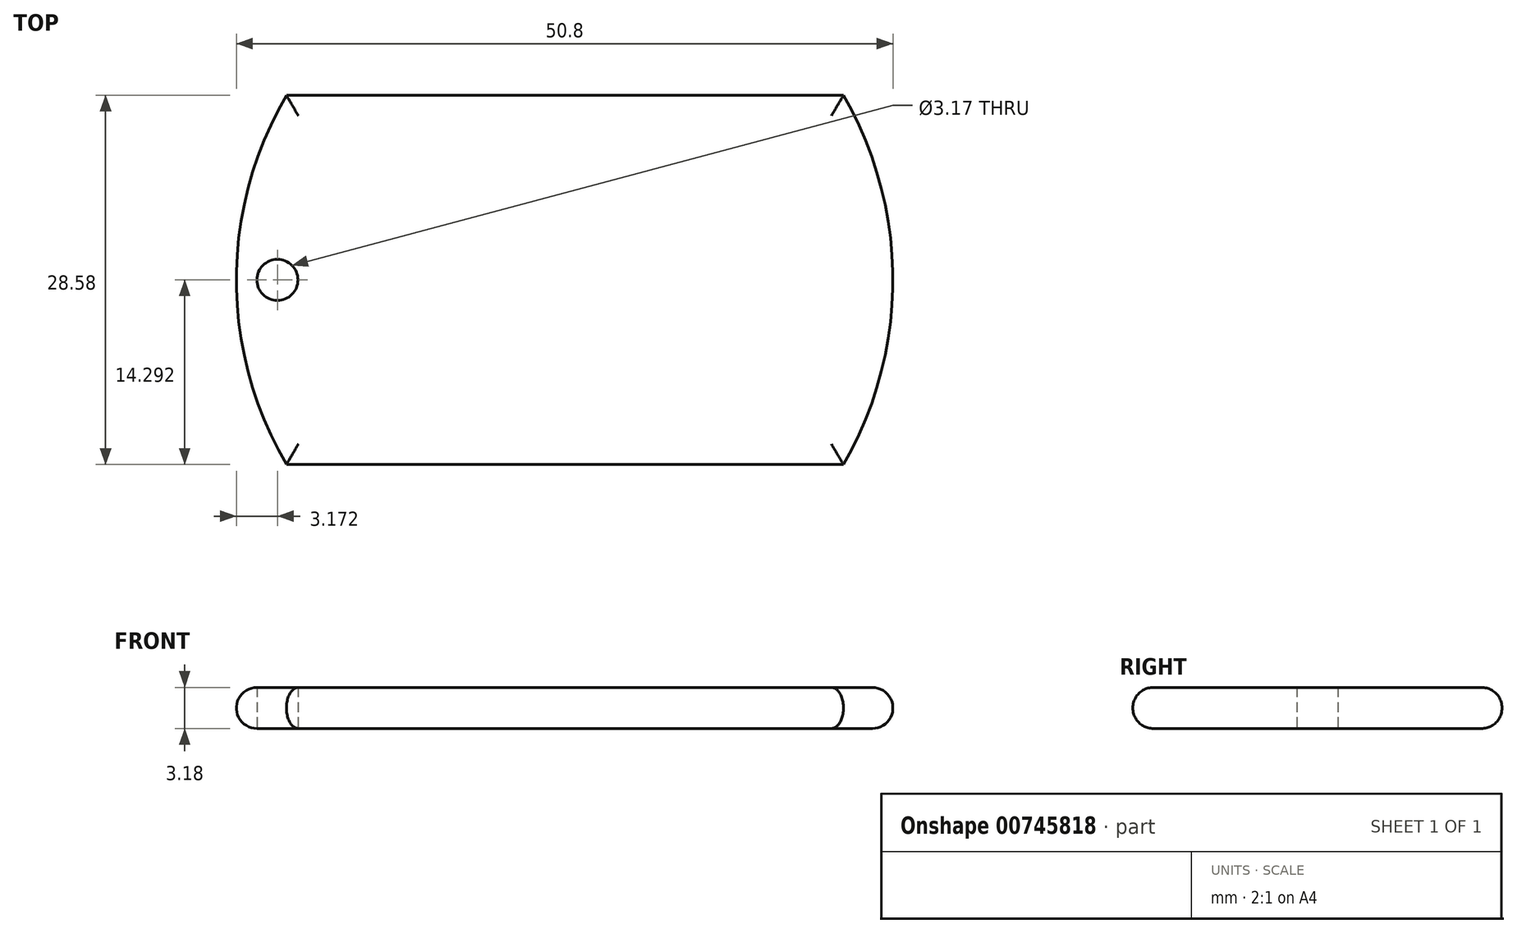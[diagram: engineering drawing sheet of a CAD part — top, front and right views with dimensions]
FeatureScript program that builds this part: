
annotation { "Feature Type Name" : "Feature", "Feature Type Description" : "" }
export const myFeature = defineFeature(function(context is Context, id is Id, definition is map)
    precondition{}
    {
        {
            var Q0;
            Q0=qCreatedBy(makeId("Top.planeOp"),FACE);
            var sketch = newSketch(context, id + "F0", { "sketchPlane" : qUnion([Q0])});
            skLineSegment(sketch, "E0.bottom", {"start": v(21.55, 14.35) * mm, "end": v(0, 14.35) * mm});
            skLineSegment(sketch, "E0.top", {"start": v(21.55, -14.23) * mm, "end": v(0, -14.23) * mm});
            skPoint(sketch, "E0.middle", {"position": v(0, 0) * mm});
            skArc(sketch, "E1", {"start": v(21.55, -14.23) * mm, "mid": v(25.38, 0.06) * mm, "end": v(21.55, 14.35) * mm});
            skLineSegment(sketch, "E2.MirrorCS", {"start": v(-21.55, -14.23) * mm, "end": v(0, -14.23) * mm});
            skLineSegment(sketch, "E3.MirrorCS", {"start": v(-21.55, 14.35) * mm, "end": v(0, 14.35) * mm});
            skArc(sketch, "E4.MirrorCS", {"start": v(-21.55, -14.23) * mm, "mid": v(-25.42, 0.06) * mm, "end": v(-21.55, 14.35) * mm});
            skLineSegment(sketch, "E5", {"start": v(-23.84, 0.06) * mm, "end": v(-22.25, 0.06) * mm});
            skCircle(sketch, "E6", {"center": v(-22.25, 0.06) * mm, "radius": 1.59 * mm});
            skSolve(sketch);
        }
        {
            var Q0;
            Q0=makeQuery(id+"F0.imprint","IMPRINT",FACE,{"disambiguationData":[TD([[makeQuery(id+"F0.imprint","IMPRINT",EDGE,{"derivedFrom":sQuery(id+"F0.wireOp",EDGE,"E0.bottom")}),1.0]])]});
            extrude(context, id + "F1", {"entities" : qUnion([Q0]), "depth" : 3.17 * mm, "offsetDistance" : 25.4 * mm});
        }
        {
            var Q0;
            Q0=makeQuery(id+"F1.opExtrude","CAP_EDGE",EDGE,{"disambiguationData":[OSD([sQuery(id+"F0.wireOp",EDGE,"E0.top"),sQuery(id+"F0.wireOp",EDGE,"E2.MirrorCS")])],"isStart":false});
            var Q1;
            Q1=makeQuery(id+"F1.opExtrude","CAP_EDGE",EDGE,{"disambiguationData":[OSD([sQuery(id+"F0.wireOp",EDGE,"E1")])],"isStart":false});
            var Q2;
            Q2=makeQuery(id+"F1.opExtrude","CAP_EDGE",EDGE,{"disambiguationData":[OSD([sQuery(id+"F0.wireOp",EDGE,"E0.bottom"),sQuery(id+"F0.wireOp",EDGE,"E3.MirrorCS")])],"isStart":false});
            var Q3;
            Q3=makeQuery(id+"F1.opExtrude","CAP_EDGE",EDGE,{"disambiguationData":[OSD([sQuery(id+"F0.wireOp",EDGE,"E4.MirrorCS")])],"isStart":false});
            var Q4;
            Q4=makeQuery(id+"F1.opExtrude","CAP_EDGE",EDGE,{"disambiguationData":[OSD([sQuery(id+"F0.wireOp",EDGE,"E0.top"),sQuery(id+"F0.wireOp",EDGE,"E2.MirrorCS")])],"isStart":true});
            var Q5;
            Q5=makeQuery(id+"F1.opExtrude","CAP_EDGE",EDGE,{"disambiguationData":[OSD([sQuery(id+"F0.wireOp",EDGE,"E4.MirrorCS")])],"isStart":true});
            var Q6;
            Q6=makeQuery(id+"F1.opExtrude","CAP_EDGE",EDGE,{"disambiguationData":[OSD([sQuery(id+"F0.wireOp",EDGE,"E0.bottom"),sQuery(id+"F0.wireOp",EDGE,"E3.MirrorCS")])],"isStart":true});
            var Q7;
            Q7=makeQuery(id+"F1.opExtrude","CAP_EDGE",EDGE,{"disambiguationData":[OSD([sQuery(id+"F0.wireOp",EDGE,"E1")])],"isStart":true});
            fillet(context, id + "F2", {"entities" : qUnion([Q0, Q1, Q2, Q3, Q4, Q5, Q6, Q7]), "radius" : 1.59 * mm, "tangentPropagation" : true, "allowEdgeOverflow" : false});
        }
    });
